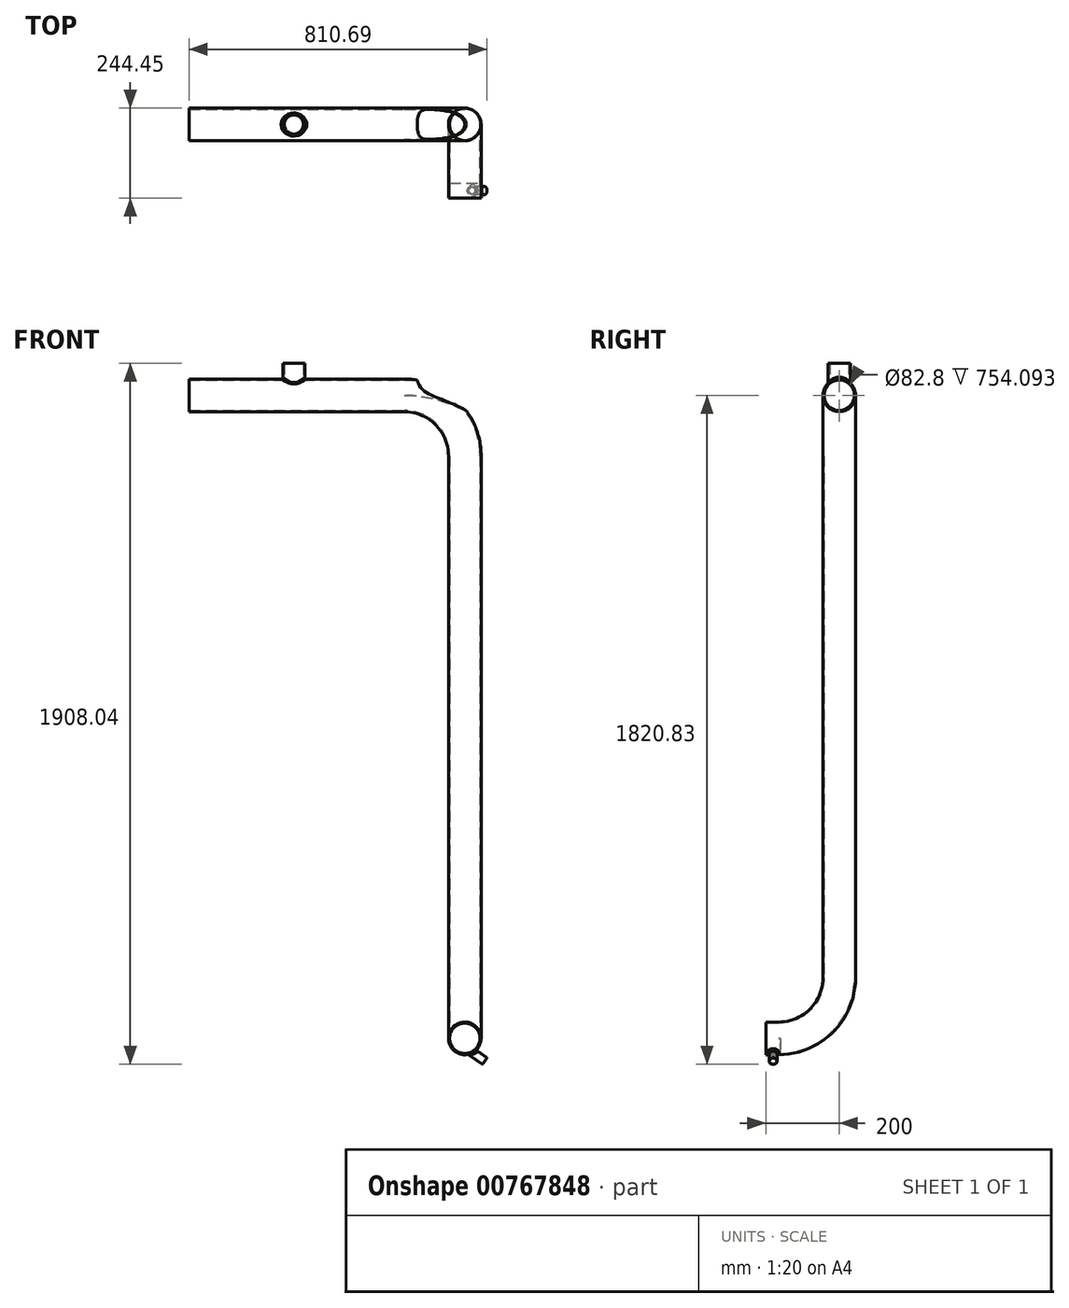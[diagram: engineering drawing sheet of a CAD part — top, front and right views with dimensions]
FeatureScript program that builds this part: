
annotation { "Feature Type Name" : "Feature", "Feature Type Description" : "" }
export const myFeature = defineFeature(function(context is Context, id is Id, definition is map)
    precondition{}
    {
        {
            var Q0;
            Q0=qCreatedBy(makeId("Front.planeOp"),FACE);
            var sketch = newSketch(context, id + "F0", { "sketchPlane" : qUnion([Q0])});
            skLineSegment(sketch, "E0", {"start": v(-165, 212.8) * mm, "end": v(-750, 212.8) * mm});
            skLineSegment(sketch, "E1", {"start": v(0, 47.8) * mm, "end": v(0, -1537.2) * mm});
            skPoint(sketch, "E2.visualSharp", {"position": v(0, 212.8) * mm});
            skArc(sketch, "E2.filletArc", {"start": v(0, 47.8) * mm, "mid": v(-48.33, 164.46) * mm, "end": v(-165, 212.8) * mm});
            skSolve(sketch);
        }
        {
            var Q0;
            Q0=qCreatedBy(makeId("Right.planeOp"),FACE);
            var Q1;
            Q1=sQuery(id+"F0.wireOp",VERTEX,"E1.end");
            cPlane(context, id + "F1", {"entities" : qUnion([Q0, Q1]), "cplaneType" : CPlaneType.PLANE_POINT, "offset" : 25 * mm, "width" : 150 * mm, "height" : 150 * mm});
        }
        {
            var Q0;
            Q0=qCreatedBy(id+"F1.planeOp",FACE);
            var sketch = newSketch(context, id + "F2", { "sketchPlane" : qUnion([Q0])});
            skLineSegment(sketch, "E3.0", {"start": v(0, 47.8) * mm, "end": v(0, -1372.2) * mm});
            skLineSegment(sketch, "E4", {"start": v(-165, -1537.2) * mm, "end": v(-200, -1537.2) * mm});
            skPoint(sketch, "E5.visualSharp", {"position": v(0, -1537.2) * mm});
            skArc(sketch, "E5.filletArc", {"start": v(-165, -1537.2) * mm, "mid": v(-48.33, -1488.88) * mm, "end": v(0, -1372.2) * mm});
            skSolve(sketch);
        }
        {
            var Q0;
            Q0=qCreatedBy(makeId("Right.planeOp"),FACE);
            var Q1;
            Q1=sQuery(id+"F0.wireOp",VERTEX,"E0.end");
            cPlane(context, id + "F3", {"entities" : qUnion([Q0, Q1]), "cplaneType" : CPlaneType.PLANE_POINT, "offset" : 25 * mm, "width" : 150 * mm, "height" : 150 * mm});
        }
        {
            var Q0;
            Q0=qCreatedBy(id+"F3.planeOp",FACE);
            var sketch = newSketch(context, id + "F4", { "sketchPlane" : qUnion([Q0])});
            skPoint(sketch, "E6.0", {"position": v(0, 212.8) * mm});
            skCircle(sketch, "E7", {"center": v(0, 212.8) * mm, "radius": 44.45 * mm});
            skCircle(sketch, "E8", {"center": v(0, 212.8) * mm, "radius": 41.4 * mm});
            skSolve(sketch);
        }
        {
            var Q0;
            Q0=makeQuery(id+"F4.imprint","IMPRINT",FACE,{"disambiguationData":[TD([[makeQuery(id+"F4.imprint","IMPRINT",EDGE,{"derivedFrom":sQuery(id+"F4.wireOp",EDGE,"E7")}),1.0]])]});
            var Q1;
            Q1=sQuery(id+"F0.wireOp",EDGE,"E0");
            var Q2;
            Q2=sQuery(id+"F0.wireOp",EDGE,"E2.filletArc");
            var Q3;
            Q3=sQuery(id+"F2.wireOp",EDGE,"E3.0");
            var Q4;
            Q4=sQuery(id+"F2.wireOp",EDGE,"E5.filletArc");
            var Q5;
            Q5=sQuery(id+"F2.wireOp",EDGE,"E4");
            sweep(context, id + "F5", {"profiles" : qUnion([Q0]), "path" : qUnion([Q1, Q2, Q3, Q4, Q5])});
        }
        {
            var Q0;
            Q0=qCreatedBy(id+"F1.planeOp",FACE);
            var Q1;
            Q1=makeQuery(id+"F5.opSweep","SWEPT_FACE",FACE,{"disambiguationData":[OSD([sQuery(id+"F2.wireOp",EDGE,"E4"),sQuery(id+"F4.wireOp",EDGE,"E7")])]});
            cPlane(context, id + "F6", {"entities" : qUnion([Q0, Q1]), "cplaneType" : CPlaneType.LINE_ANGLE, "offset" : 25 * mm, "angle" : 35 * degree, "oppositeDirection" : true, "width" : 150 * mm, "height" : 150 * mm});
        }
        {
            var Q0;
            Q0=qCreatedBy(id+"F6.planeOp",FACE);
            var sketch = newSketch(context, id + "F7", { "sketchPlane" : qUnion([Q0])});
            skCircle(sketch, "E9", {"center": v(180, -1278.66) * mm, "radius": 10 * mm});
            skCircle(sketch, "E10", {"center": v(180, -1278.66) * mm, "radius": 11 * mm});
            skLineSegment(sketch, "E11", {"start": v(300, -1303.66) * mm, "end": v(165, -1303.66) * mm});
            skSolve(sketch);
        }
        {
            var Q0;
            Q0 = qSketchRegion(id + "F7", true);
            extrude(context, id + "F8", {"entities" : qUnion([Q0]), "operationType" : NewBodyOperationType.ADD, "oppositeDirection" : true, "depth" : 80 * mm, "offsetDistance" : 25 * mm});
        }
        {
            var Q0;
            Q0=makeQuery(id+"F5.opSweep","CAP_FACE",FACE,{"disambiguationData":[OSD([sQuery(id+"F2.wireOp",VERTEX,"E4.end"),sQuery(id+"F4.wireOp",EDGE,"E7"),sQuery(id+"F4.wireOp",EDGE,"E8")])],"isStart":false});
            var sketch = newSketch(context, id + "F9", { "sketchPlane" : qUnion([Q0])});
            skCircle(sketch, "E12.0", {"center": v(0, -1537.2) * mm, "radius": 41.4 * mm});
            skSolve(sketch);
        }
        {
            var Q0;
            Q0=makeQuery(id+"F9.imprint","IMPRINT",FACE,{"disambiguationData":[TD([[makeQuery(id+"F9.imprint","IMPRINT",EDGE,{"derivedFrom":sQuery(id+"F9.wireOp",EDGE,"E12.0")}),1.0]])]});
            extrude(context, id + "F10", {"entities" : qUnion([Q0]), "operationType" : NewBodyOperationType.REMOVE, "oppositeDirection" : true, "depth" : 40 * mm, "offsetDistance" : 25 * mm});
        }
        {
            var Q0;
            Q0=makeQuery(id+"F8.opExtrude","CAP_FACE",FACE,{"disambiguationData":[OSD([sQuery(id+"F7.wireOp",EDGE,"E9"),sQuery(id+"F7.wireOp",EDGE,"E10")])],"isStart":false});
            var sketch = newSketch(context, id + "F11", { "sketchPlane" : qUnion([Q0])});
            skCircle(sketch, "E13.0", {"center": v(-180, -1278.66) * mm, "radius": 10 * mm});
            skSolve(sketch);
        }
        {
            var Q0;
            Q0 = qSketchRegion(id + "F11", true);
            extrude(context, id + "F12", {"entities" : qUnion([Q0]), "operationType" : NewBodyOperationType.REMOVE, "oppositeDirection" : true, "depth" : 100 * mm, "offsetDistance" : 25 * mm});
        }
        {
            var Q0;
            Q0=qCreatedBy(makeId("Top.planeOp"),FACE);
            cPlane(context, id + "F13", {"entities" : qUnion([Q0]), "cplaneType" : CPlaneType.OFFSET, "offset" : 200 * mm, "width" : 150 * mm, "height" : 150 * mm});
        }
        {
            var Q0;
            Q0=qCreatedBy(id+"F13.planeOp",FACE);
            var sketch = newSketch(context, id + "F14", { "sketchPlane" : qUnion([Q0])});
            skCircle(sketch, "E14", {"center": v(-465, 0) * mm, "radius": 30.15 * mm});
            skCircle(sketch, "E15", {"center": v(-465, 0) * mm, "radius": 26 * mm});
            skSolve(sketch);
        }
        {
            var Q0;
            Q0 = qSketchRegion(id + "F14", true);
            extrude(context, id + "F15", {"entities" : qUnion([Q0]), "operationType" : NewBodyOperationType.ADD, "depth" : 100 * mm, "offsetDistance" : 25 * mm});
        }
        {
            var Q0;
            Q0=qCreatedBy(id+"F3.planeOp",FACE);
            var sketch = newSketch(context, id + "F16", { "sketchPlane" : qUnion([Q0])});
            skCircle(sketch, "E16.0", {"center": v(0, 212.8) * mm, "radius": 41.4 * mm});
            skSolve(sketch);
        }
        {
            var Q0;
            Q0 = qSketchRegion(id + "F16", true);
            extrude(context, id + "F17", {"entities" : qUnion([Q0]), "operationType" : NewBodyOperationType.REMOVE, "depth" : 800 * mm, "offsetDistance" : 25 * mm});
        }
        {
            var Q0;
            Q0=makeQuery(id+"F15.opExtrude","CAP_FACE",FACE,{"disambiguationData":[OSD([sQuery(id+"F14.wireOp",EDGE,"E14"),sQuery(id+"F14.wireOp",EDGE,"E15")])],"isStart":false});
            var sketch = newSketch(context, id + "F18", { "sketchPlane" : qUnion([Q0])});
            skCircle(sketch, "E17.0", {"center": v(-465, 0) * mm, "radius": 26 * mm});
            skSolve(sketch);
        }
        {
            var Q0;
            Q0 = qSketchRegion(id + "F18", true);
            extrude(context, id + "F19", {"entities" : qUnion([Q0]), "operationType" : NewBodyOperationType.REMOVE, "oppositeDirection" : true, "depth" : 100 * mm, "offsetDistance" : 25 * mm});
        }
        {
            var Q0;
            Q0=makeQuery(id+"F15.boolean.opBoolean","INTERSECT",EDGE,{"derivedFrom":[makeQuery(id+"F5.opSweep","SWEPT_FACE",FACE,{"disambiguationData":[OSD([sQuery(id+"F0.wireOp",EDGE,"E0"),sQuery(id+"F4.wireOp",EDGE,"E7")])]}),makeQuery(id+"F15.opExtrude","SWEPT_FACE",FACE,{"disambiguationData":[OSD([sQuery(id+"F14.wireOp",EDGE,"E14")])]})]});
            var Q1;
            Q1=makeQuery(id+"F8.boolean.opBoolean","INTERSECT",EDGE,{"derivedFrom":[makeQuery(id+"F5.opSweep","SWEPT_FACE",FACE,{"disambiguationData":[OSD([sQuery(id+"F2.wireOp",EDGE,"E4"),sQuery(id+"F4.wireOp",EDGE,"E7")])]}),makeQuery(id+"F8.opExtrude","SWEPT_FACE",FACE,{"disambiguationData":[OSD([sQuery(id+"F7.wireOp",EDGE,"E10")])]})]});
            fillet(context, id + "F20", {"entities" : qUnion([Q0, Q1]), "radius" : 5 * mm, "tangentPropagation" : true, "allowEdgeOverflow" : false});
        }
    });
